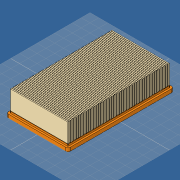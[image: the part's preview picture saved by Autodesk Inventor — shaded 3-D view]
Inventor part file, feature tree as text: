
AUTODESK INVENTOR PART (.ipt)
format: ipt  version: 2019 (Build 230136000, 136)  size: 351,232 bytes
history: native  units: mm
features: extrude x3, sketch x2, pattern_linear x2, chamfer x1, other x1
ambient origin geometry x8: Origin, YZ Plane, XZ Plane, XY Plane, X Axis, Y Axis, Z Axis, Center Point
bodies: Volumenkörper1 (feature_tree)
feature tree (9):
  sketch  "Skizze1"  dims[d0=140.0mm d1=240.0mm]
  extrude  "Extrusion1"  Depth=240.0mm
  extrude  "Extrusion2"  Depth=232.0mm
  chamfer  "Fase1"  Distance=132.0mm
  extrude  "Extrusion3"  Depth=2.0mm
  pattern_linear  "Rechteckige Anordnung1"  Spacing1=8.0mm  [1 undecoded]
  pattern_linear  "Rechteckige Anordnung2"  Spacing1=4.0mm  [1 undecoded]
  sketch  "Skizze2"  dims[d2=5.0mm d3=232.0mm d4=132.0mm d5=2.0mm d6=8.0mm d7=0.0mm d8=4.0mm d9=0.0mm d10=120.0mm d11=220.0mm d12=2.0mm d13=4.0mm d14=2.0mm d15=45.0deg d16=44.0mm d17=2.0mm d18=130.0mm d19=0.0mm d20=360.0mm d22=114.0mm d23=360.0mm d25=114.0mm]
  other  "Schnittkanten projizieren1"
note: 2 required parameter values undecoded (feature->parameter linkage not recoverable at this tier; creation-order binding heuristic only, values carry confidence <= 0.55)
